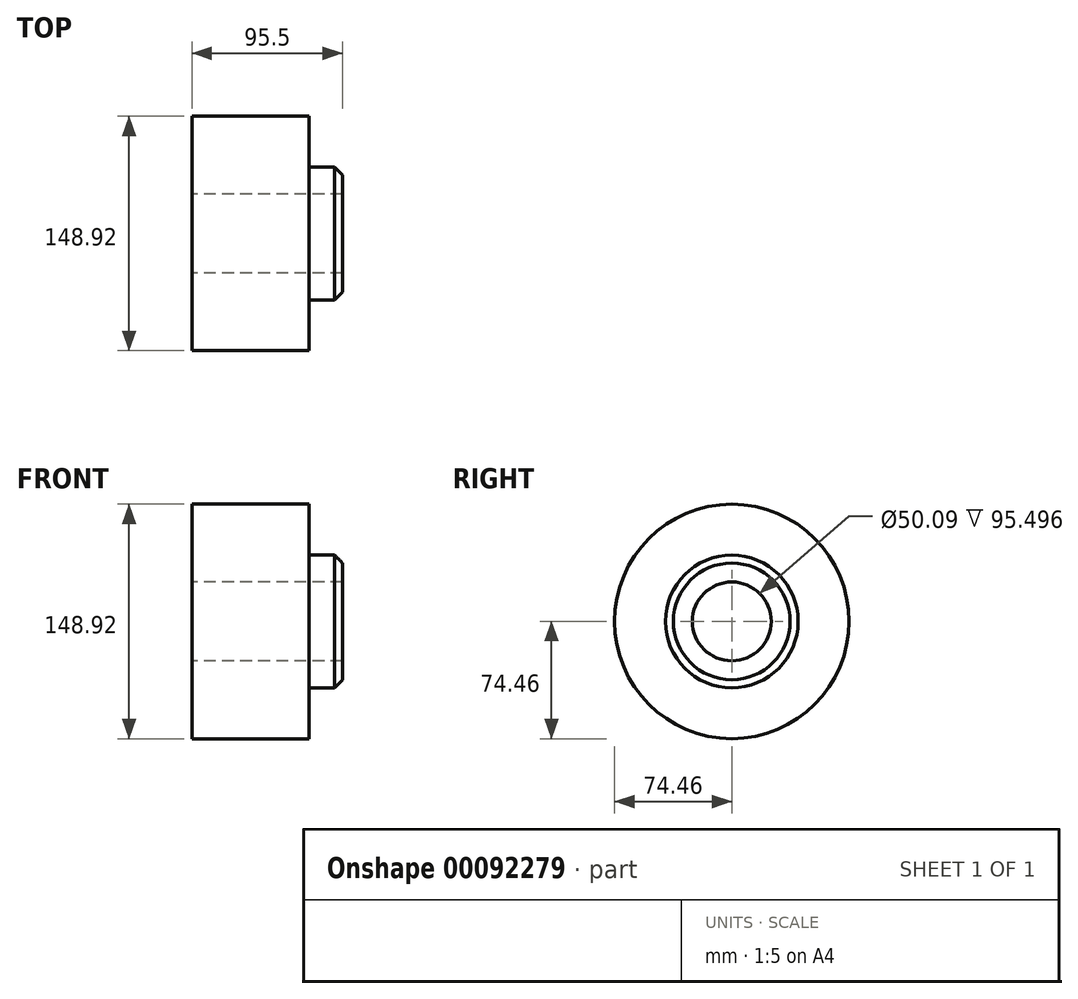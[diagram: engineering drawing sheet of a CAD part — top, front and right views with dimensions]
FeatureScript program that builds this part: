
annotation { "Feature Type Name" : "Feature", "Feature Type Description" : "" }
export const myFeature = defineFeature(function(context is Context, id is Id, definition is map)
    precondition{}
    {
        {
            var Q0;
            Q0=qCreatedBy(makeId("Front.planeOp"),FACE);
            var sketch = newSketch(context, id + "F0", { "sketchPlane" : qUnion([Q0])});
            skLineSegment(sketch, "E0.bottom", {"start": v(0, 25.05) * mm, "end": v(22.54, 25.05) * mm});
            skLineSegment(sketch, "E0.top", {"start": v(0, 74.46) * mm, "end": v(22.54, 74.46) * mm});
            skLineSegment(sketch, "E0.left", {"start": v(0, 25.05) * mm, "end": v(0, 74.46) * mm});
            skLineSegment(sketch, "E0.right", {"start": v(22.54, 25.05) * mm, "end": v(22.54, 74.46) * mm});
            skLineSegment(sketch, "E1.bottom", {"start": v(0, 25.05) * mm, "end": v(43.9, 25.05) * mm});
            skLineSegment(sketch, "E1.top", {"start": v(0, 42.14) * mm, "end": v(43.9, 42.14) * mm});
            skLineSegment(sketch, "E1.left", {"start": v(0, 25.05) * mm, "end": v(0, 42.14) * mm});
            skLineSegment(sketch, "E1.right", {"start": v(43.9, 25.05) * mm, "end": v(43.9, 42.14) * mm});
            skLineSegment(sketch, "E2", {"start": v(0, 0) * mm, "end": v(45.14, 0) * mm});
            skSolve(sketch);
        }
        {
            var Q0;
            Q0 = qSketchRegion(id + "F0", true);
            var Q1;
            Q1=sQuery(id+"F0.wireOp",EDGE,"E2");
            revolve(context, id + "F1", {"entities" : qUnion([Q0]), "axis" : qUnion([Q1]), "revolveType" : RevolveType.FULL});
        }
        {
            var Q0;
            Q0=makeQuery(id+"F1.opRevolve","SWEPT_FACE",FACE,{"disambiguationData":[OSD([sQuery(id+"F0.wireOp",EDGE,"E0.left"),sQuery(id+"F0.wireOp",EDGE,"E1.left")])]});
            extrude(context, id + "F2", {"entities" : qUnion([Q0]), "operationType" : NewBodyOperationType.ADD, "depth" : 51.6 * mm});
        }
        {
            var Q0;
            Q0=makeQuery(id+"F1.opRevolve","SWEPT_EDGE",EDGE,{"disambiguationData":[OSD([sQuery(id+"F0.wireOp",EDGE,"E1.top"),sQuery(id+"F0.wireOp",EDGE,"E1.right")])]});
            chamfer(context, id + "F4", {"entities" : qUnion([Q0]), "width" : 5.08 * mm, "tangentPropagation" : true});
        }
    });
